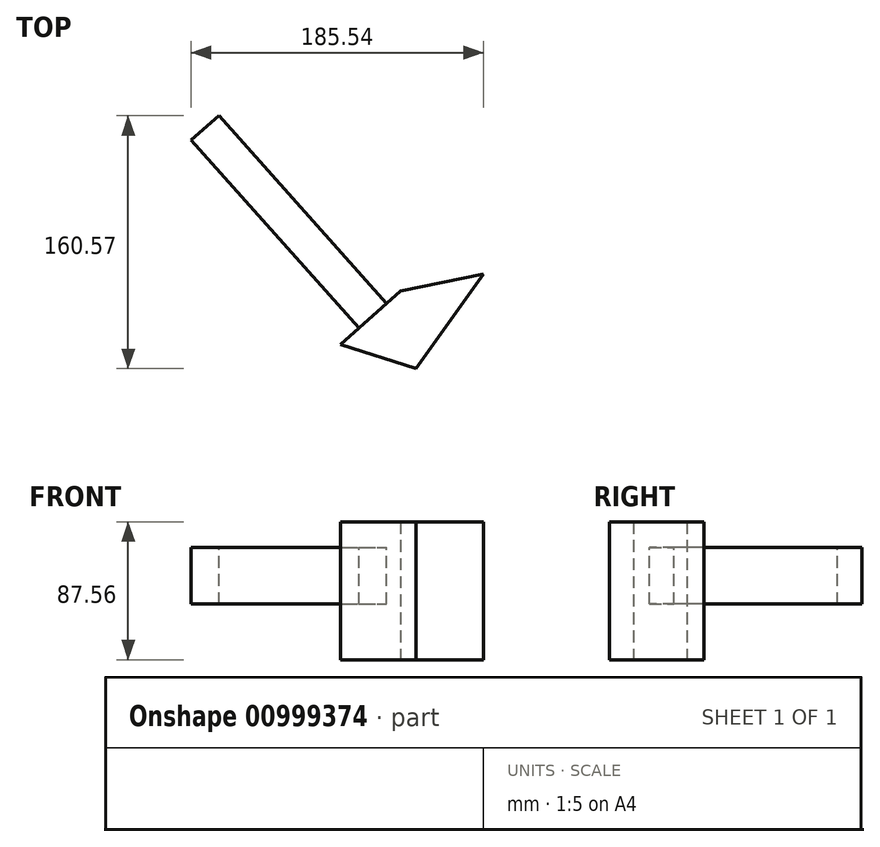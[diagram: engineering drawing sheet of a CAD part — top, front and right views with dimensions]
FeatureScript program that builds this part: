
annotation { "Feature Type Name" : "Feature", "Feature Type Description" : "" }
export const myFeature = defineFeature(function(context is Context, id is Id, definition is map)
    precondition{}
    {
        {
            var Q0;
            Q0=qCreatedBy(makeId("Top.planeOp"),FACE);
            var sketch = newSketch(context, id + "F0", { "sketchPlane" : qUnion([Q0])});
            skLineSegment(sketch, "E0", {"start": v(0, 21.4) * mm, "end": v(-38.26, -12.7) * mm});
            skLineSegment(sketch, "E1", {"start": v(-38.26, -12.7) * mm, "end": v(9.79, -27.86) * mm});
            skLineSegment(sketch, "E2", {"start": v(9.79, -27.86) * mm, "end": v(52.53, 32.23) * mm});
            skLineSegment(sketch, "E3", {"start": v(52.53, 32.23) * mm, "end": v(0, 21.4) * mm});
            skSolve(sketch);
        }
        {
            var Q0;
            Q0=makeQuery(id+"F0.imprint","IMPRINT",FACE,{"disambiguationData":[TD([[makeQuery(id+"F0.imprint","IMPRINT",EDGE,{"derivedFrom":sQuery(id+"F0.wireOp",EDGE,"E0")}),1.0]])]});
            extrude(context, id + "F1", {"entities" : qUnion([Q0]), "depth" : 87.56 * mm, "offsetDistance" : 25.4 * mm});
        }
        {
            var Q0;
            Q0=makeQuery(id+"F1.opExtrude","SWEPT_FACE",FACE,{"disambiguationData":[OSD([sQuery(id+"F0.wireOp",EDGE,"E0")])]});
            var sketch = newSketch(context, id + "F2", { "sketchPlane" : qUnion([Q0])});
            skLineSegment(sketch, "E4.bottom", {"start": v(21.4, 35.4) * mm, "end": v(-2.07, 35.4) * mm});
            skLineSegment(sketch, "E4.top", {"start": v(21.4, 71.52) * mm, "end": v(-2.07, 71.52) * mm});
            skLineSegment(sketch, "E4.left", {"start": v(21.4, 35.4) * mm, "end": v(21.4, 71.52) * mm});
            skLineSegment(sketch, "E4.right", {"start": v(-2.07, 35.4) * mm, "end": v(-2.07, 71.52) * mm});
            skPoint(sketch, "E4.middle", {"position": v(9.67, 53.46) * mm});
            skSolve(sketch);
        }
        {
            var Q0;
            Q0=makeQuery(id+"F2.imprint","IMPRINT",FACE,{"disambiguationData":[TD([[makeQuery(id+"F2.imprint","IMPRINT",EDGE,{"derivedFrom":sQuery(id+"F2.wireOp",EDGE,"E4.bottom")}),-1.0]])]});
            extrude(context, id + "F3", {"entities" : qUnion([Q0]), "operationType" : NewBodyOperationType.ADD, "depth" : 159.94 * mm, "offsetDistance" : 25.4 * mm});
        }
    });
